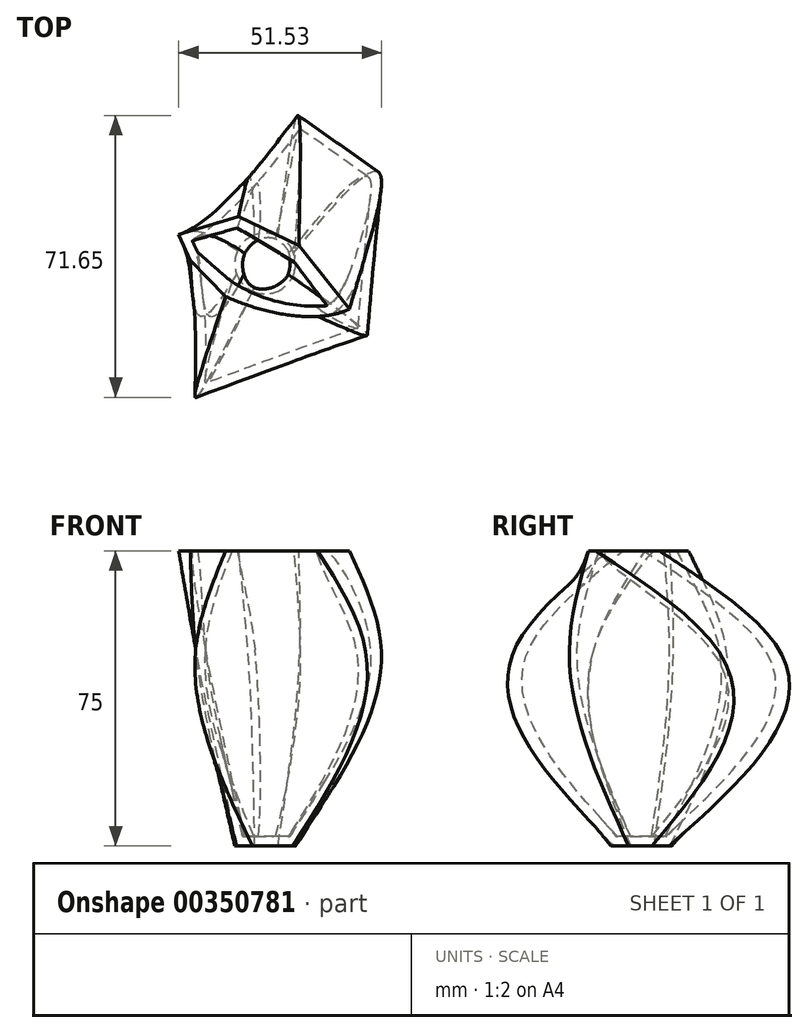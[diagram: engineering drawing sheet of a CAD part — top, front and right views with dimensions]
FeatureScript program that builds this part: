
annotation { "Feature Type Name" : "Feature", "Feature Type Description" : "" }
export const myFeature = defineFeature(function(context is Context, id is Id, definition is map)
    precondition{}
    {
        {
            var Q0;
            Q0=qCreatedBy(makeId("Top.planeOp"),FACE);
            var sketch = newSketch(context, id + "F0", { "sketchPlane" : qUnion([Q0])});
            skCircle(sketch, "E0", {"center": v(0, 0) * mm, "radius": 7.73 * mm});
            skSolve(sketch);
        }
        {
            var Q0;
            Q0=qCreatedBy(makeId("Top.planeOp"),FACE);
            cPlane(context, id + "F1", {"entities" : qUnion([Q0]), "cplaneType" : CPlaneType.OFFSET, "offset" : 50 * mm, "width" : 150 * mm, "height" : 150 * mm});
        }
        {
            var Q0;
            Q0=qCreatedBy(id+"F1.planeOp",FACE);
            var sketch = newSketch(context, id + "F2", { "sketchPlane" : qUnion([Q0])});
            skLineSegment(sketch, "E1", {"start": v(-17.63, 8.14) * mm, "end": v(-17.63, -32.22) * mm});
            skLineSegment(sketch, "E2", {"start": v(-17.63, -32.22) * mm, "end": v(25.43, -18.31) * mm});
            skLineSegment(sketch, "E3", {"start": v(25.43, -18.31) * mm, "end": v(29.5, 19.33) * mm});
            skLineSegment(sketch, "E4", {"start": v(29.5, 19.33) * mm, "end": v(8.82, 34.93) * mm});
            skLineSegment(sketch, "E5", {"start": v(8.82, 34.93) * mm, "end": v(-17.63, 8.14) * mm});
            skSolve(sketch);
        }
        {
            var Q0;
            Q0=qCreatedBy(id+"F1.planeOp",FACE);
            cPlane(context, id + "F3", {"entities" : qUnion([Q0]), "cplaneType" : CPlaneType.OFFSET, "offset" : 25 * mm, "width" : 150 * mm, "height" : 150 * mm});
        }
        {
            var Q0;
            Q0=qCreatedBy(id+"F3.planeOp",FACE);
            var sketch = newSketch(context, id + "F4", { "sketchPlane" : qUnion([Q0])});
            skEllipse(sketch, "E6", {"center": v(0, 0) * mm, "majorRadius": 25.92 * mm, "minorRadius": 11.47 * mm, "majorAxis": v(0.95, -0.3)});
            skLineSegment(sketch, "E7", {"start": v(-6.72, 11.97) * mm, "end": v(-21.97, 7.3) * mm});
            skLineSegment(sketch, "E8", {"start": v(-19.04, 0.91) * mm, "end": v(-7.14, -11.37) * mm});
            skLineSegment(sketch, "E9", {"start": v(-19.04, 0.91) * mm, "end": v(-21.97, 7.3) * mm});
            skLineSegment(sketch, "E10", {"start": v(-7.14, -11.37) * mm, "end": v(23.8, -14.51) * mm});
            skLineSegment(sketch, "E11", {"start": v(23.8, -14.51) * mm, "end": v(8.54, 4.53) * mm});
            skLineSegment(sketch, "E12", {"start": v(8.54, 4.53) * mm, "end": v(-6.72, 11.97) * mm});
            skSolve(sketch);
        }
        {
            var Q0;
            Q0=makeQuery(id+"F0.imprint","IMPRINT",FACE,{"disambiguationData":[TD([[makeQuery(id+"F0.imprint","IMPRINT",EDGE,{"derivedFrom":sQuery(id+"F0.wireOp",EDGE,"E0")}),1.0]])]});
            var Q1;
            Q1=makeQuery(id+"F2.imprint","IMPRINT",FACE,{"disambiguationData":[TD([[makeQuery(id+"F2.imprint","IMPRINT",EDGE,{"derivedFrom":sQuery(id+"F2.wireOp",EDGE,"E1")}),1.0]])]});
            var Q2;
            Q2=makeQuery(id+"F4.imprint","IMPRINT",FACE,{"disambiguationData":[TD([[makeQuery(id+"F4.imprint","IMPRINT",EDGE,{"derivedFrom":sQuery(id+"F4.wireOp",EDGE,"E6")}),1.0]])]});
            loft(context, id + "F5", {"sheetProfilesArray" : [{ "sheetProfileEntities" : qUnion([Q0]) }, { "sheetProfileEntities" : qUnion([Q1]) }, { "sheetProfileEntities" : qUnion([Q2]) }]});
        }
        {
            var Q0;
            Q0=makeQuery(id+"F5.opLoft","CAP_FACE",FACE,{"disambiguationData":[OSD([makeQuery(id+"F4.imprint","IMPRINT",FACE,{"disambiguationData":[TD([[makeQuery(id+"F4.imprint","IMPRINT",EDGE,{"derivedFrom":sQuery(id+"F4.wireOp",EDGE,"E6")}),1.0]])]})])],"isStart":true});
            shell(context, id + "F6", {"entities" : qUnion([Q0]), "thickness" : 2.5 * mm});
        }
    });
